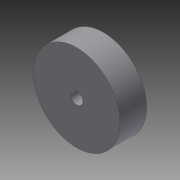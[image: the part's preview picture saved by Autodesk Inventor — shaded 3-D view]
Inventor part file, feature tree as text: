
AUTODESK INVENTOR PART (.ipt)
format: ipt  version: 2015 (Build 190159000, 159)  size: 76,800 bytes
history: native  units: mm
features: extrude x1, sketch x1
ambient origin geometry x8: Origin, YZ Plane, XZ Plane, XY Plane, X Axis, Y Axis, Z Axis, Center Point
bodies: Solid1 (feature_tree)
feature tree (2):
  extrude  "Extrusion1"  Depth=6.0mm
  sketch  "Sketch1"  dims[d0=2.8mm d2=19.5mm d3=6.0mm d4=0.0mm]
